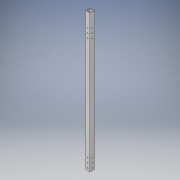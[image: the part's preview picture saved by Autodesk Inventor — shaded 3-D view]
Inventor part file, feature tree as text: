
AUTODESK INVENTOR PART (.ipt)
format: ipt  version: 2018 (Build 220112000, 112)  size: 156,672 bytes
history: native  units: in
note: dims shown in document units (in); Inventor stores cm internally (conversion verified against a paired STEP export)
features: extrude x3, sketch x3
ambient origin geometry x8: Origin, YZ Plane, XZ Plane, XY Plane, X Axis, Y Axis, Z Axis, Center Point
bodies: Solid1 (feature_tree)
feature tree (6):
  extrude  "Extrusion1"  Depth=1.0in
  extrude  "Extrusion2"  Depth=30.0in TaperAngle=0.0deg
  extrude  "Extrusion3"  Depth=30.0in
  sketch  "Sketch1"  dims[d0=1.0in d1=1.0in]
  sketch  "Sketch2"  dims[d2=0.125in d3=30.0in d4=0.0in]
  sketch  "Sketch3"  dims[d6=0.2031in d8=0.2031in d9=1.0in d10=1.0in d11=0.2031in d12=0.2031in d13=1.0in d14=1.0in d15=0.2031in d16=0.2031in d17=30.0in d18=0.0in d19=0.5in d20=1.0in d21=1.0in d22=0.2031in d23=0.2031in d24=0.2031in d25=1.0in d26=1.0in d27=0.2031in d28=0.2031in d29=0.2031in d30=30.0in d31=0.0in]
